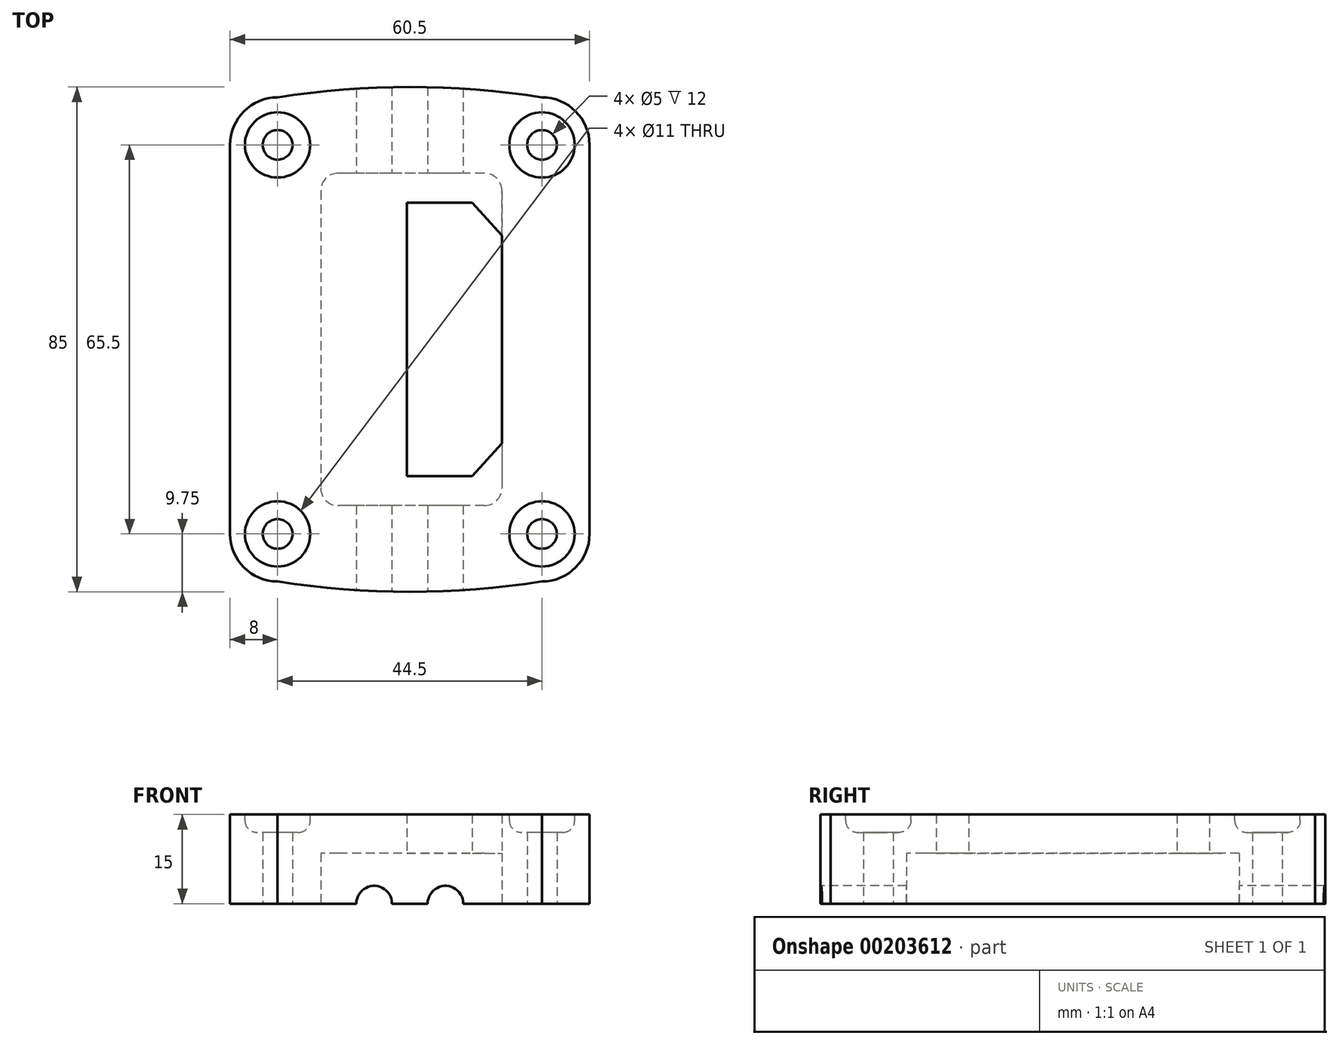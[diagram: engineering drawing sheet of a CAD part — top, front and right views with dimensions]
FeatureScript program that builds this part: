
annotation { "Feature Type Name" : "Feature", "Feature Type Description" : "" }
export const myFeature = defineFeature(function(context is Context, id is Id, definition is map)
    precondition{}
    {
        {
            var Q0;
            Q0=qCreatedBy(makeId("Top.planeOp"),FACE);
            var sketch = newSketch(context, id + "F0", { "sketchPlane" : qUnion([Q0])});
            skPoint(sketch, "E0.middle", {"position": v(0, 0) * mm});
            skCircle(sketch, "E1", {"center": v(22.25, 32.75) * mm, "radius": 2.5 * mm});
            skCircle(sketch, "E2", {"center": v(-22.25, 32.75) * mm, "radius": 2.5 * mm});
            skCircle(sketch, "E3", {"center": v(22.25, -32.75) * mm, "radius": 2.5 * mm});
            skCircle(sketch, "E4", {"center": v(-22.25, -32.75) * mm, "radius": 2.5 * mm});
            skLineSegment(sketch, "E5", {"start": v(30.25, 32.75) * mm, "end": v(30.25, -32.75) * mm});
            skLineSegment(sketch, "E6", {"start": v(-30.25, 32.75) * mm, "end": v(-30.25, -32.75) * mm});
            skArc(sketch, "E7", {"start": v(30.25, 32.75) * mm, "mid": v(27.9, 38.4) * mm, "end": v(22.25, 40.75) * mm});
            skArc(sketch, "E8", {"start": v(-30.25, 32.75) * mm, "mid": v(-27.9, 38.4) * mm, "end": v(-22.25, 40.75) * mm});
            skArc(sketch, "E9", {"start": v(30.25, -32.75) * mm, "mid": v(27.9, -38.4) * mm, "end": v(22.25, -40.75) * mm});
            skArc(sketch, "E10", {"start": v(-30.25, -32.75) * mm, "mid": v(-27.9, -38.4) * mm, "end": v(-22.25, -40.75) * mm});
            skCircle(sketch, "E11", {"center": v(22.25, 32.75) * mm, "radius": 5.5 * mm});
            skCircle(sketch, "E12", {"center": v(-22.25, 32.75) * mm, "radius": 5.5 * mm});
            skCircle(sketch, "E13", {"center": v(22.25, -32.75) * mm, "radius": 5.5 * mm});
            skCircle(sketch, "E14", {"center": v(-22.25, -32.75) * mm, "radius": 5.5 * mm});
            skArc(sketch, "E15", {"start": v(-22.25, -40.75) * mm, "mid": v(0, -42.5) * mm, "end": v(22.25, -40.75) * mm});
            skArc(sketch, "E16", {"start": v(22.25, 40.75) * mm, "mid": v(0, 42.5) * mm, "end": v(-22.25, 40.75) * mm});
            skSolve(sketch);
        }
        {
            var Q0;
            {var subQ6=sQuery(id+"F0.wireOp",EDGE,"DUTKuPmr-ej0r-RtgJ-FTay-jEPyzrQACdq5");var subQ10=sQuery(id+"F0.wireOp",EDGE,"E0.bottom");var subQ13=makeQuery(id+"F0.imprint","INTERSECT",VERTEX,{"derivedFrom":[subQ10,subQ6]});Q0=makeQuery(id+"F0.imprint","IMPRINT",FACE,{"disambiguationData":[TD([[makeQuery(id+"F0.imprint","IMPRINT",EDGE,{"disambiguationData":[TD([[subQ13,-1.0]])],"derivedFrom":subQ10}),1.0]])]});}
            var Q1;
            {var subQ0=sQuery(id+"F0.wireOp",EDGE,"E1");var subQ1=sQuery(id+"F0.wireOp",EDGE,"E0.bottom");var subQ2=makeQuery(id+"F0.imprint","INTERSECT",VERTEX,{"derivedFrom":[subQ1,subQ0]});Q1=makeQuery(id+"F0.imprint","IMPRINT",FACE,{"disambiguationData":[TD([[makeQuery(id+"F0.imprint","IMPRINT",EDGE,{"disambiguationData":[TD([[subQ2,-1.0]])],"derivedFrom":subQ1}),1.0]])]});}
            var Q2;
            {var subQ0=sQuery(id+"F0.wireOp",EDGE,"E7");Q2=makeQuery(id+"F0.imprint","IMPRINT",FACE,{"disambiguationData":[TD([[makeQuery(id+"F0.imprint","IMPRINT",EDGE,{"derivedFrom":subQ0}),1.0]])]});}
            var Q3;
            {var subQ0=sQuery(id+"F0.wireOp",EDGE,"E8");Q3=makeQuery(id+"F0.imprint","IMPRINT",FACE,{"disambiguationData":[TD([[makeQuery(id+"F0.imprint","IMPRINT",EDGE,{"derivedFrom":subQ0}),-1.0]])]});}
            var Q4;
            {var subQ5=sQuery(id+"F0.wireOp",EDGE,"E6");Q4=makeQuery(id+"F0.imprint","IMPRINT",FACE,{"disambiguationData":[TD([[makeQuery(id+"F0.imprint","IMPRINT",EDGE,{"derivedFrom":subQ5}),1.0]])]});}
            var Q5;
            {var subQ12=sQuery(id+"F0.wireOp",EDGE,"E5");Q5=makeQuery(id+"F0.imprint","IMPRINT",FACE,{"disambiguationData":[TD([[makeQuery(id+"F0.imprint","IMPRINT",EDGE,{"derivedFrom":subQ12}),-1.0]])]});}
            var Q6;
            Q6=makeQuery(id+"F0.imprint","IMPRINT",FACE,{"disambiguationData":[TD([[makeQuery(id+"F0.imprint","IMPRINT",EDGE,{"derivedFrom":sQuery(id+"F0.wireOp",EDGE,"E2")}),-1.0]])]});
            var Q7;
            Q7=makeQuery(id+"F0.imprint","IMPRINT",FACE,{"disambiguationData":[TD([[makeQuery(id+"F0.imprint","IMPRINT",EDGE,{"derivedFrom":sQuery(id+"F0.wireOp",EDGE,"E1")}),-1.0]])]});
            var Q8;
            Q8=makeQuery(id+"F0.imprint","IMPRINT",FACE,{"disambiguationData":[TD([[makeQuery(id+"F0.imprint","IMPRINT",EDGE,{"derivedFrom":sQuery(id+"F0.wireOp",EDGE,"E3")}),-1.0]])]});
            var Q9;
            Q9=makeQuery(id+"F0.imprint","IMPRINT",FACE,{"disambiguationData":[TD([[makeQuery(id+"F0.imprint","IMPRINT",EDGE,{"derivedFrom":sQuery(id+"F0.wireOp",EDGE,"E4")}),-1.0]])]});
            extrude(context, id + "F1", {"entities" : qUnion([Q0, Q1, Q2, Q3, Q4, Q5, Q6, Q7, Q8, Q9]), "depth" : 15 * mm});
        }
        {
            var Q0;
            Q0=makeQuery(id+"F1.opExtrude","CAP_FACE",FACE,{"disambiguationData":[OSD([sQuery(id+"F0.wireOp",EDGE,"E1"),sQuery(id+"F0.wireOp",EDGE,"E2"),sQuery(id+"F0.wireOp",EDGE,"E3"),sQuery(id+"F0.wireOp",EDGE,"E4"),sQuery(id+"F0.wireOp",EDGE,"E5"),sQuery(id+"F0.wireOp",EDGE,"E6"),sQuery(id+"F0.wireOp",EDGE,"E7"),sQuery(id+"F0.wireOp",EDGE,"E8"),sQuery(id+"F0.wireOp",EDGE,"E9"),sQuery(id+"F0.wireOp",EDGE,"E10"),sQuery(id+"F0.wireOp",EDGE,"E15"),sQuery(id+"F0.wireOp",EDGE,"E16")])],"isStart":false});
            var sketch = newSketch(context, id + "F2", { "sketchPlane" : qUnion([Q0])});
            skCircle(sketch, "E17.0", {"center": v(-22.25, 32.75) * mm, "radius": 5.5 * mm});
            skCircle(sketch, "E18.0", {"center": v(22.25, 32.75) * mm, "radius": 5.5 * mm});
            skCircle(sketch, "E19.0", {"center": v(-22.25, -32.75) * mm, "radius": 5.5 * mm});
            skCircle(sketch, "E20.0", {"center": v(22.25, -32.75) * mm, "radius": 5.5 * mm});
            skSolve(sketch);
        }
        {
            var Q0;
            Q0=makeQuery(id+"F2.imprint","IMPRINT",FACE,{"disambiguationData":[TD([[makeQuery(id+"F2.imprint","IMPRINT",EDGE,{"derivedFrom":sQuery(id+"F2.wireOp",EDGE,"E17.0")}),1.0]])]});
            var Q1;
            Q1=makeQuery(id+"F2.imprint","IMPRINT",FACE,{"disambiguationData":[TD([[makeQuery(id+"F2.imprint","IMPRINT",EDGE,{"derivedFrom":sQuery(id+"F2.wireOp",EDGE,"E18.0")}),1.0]])]});
            var Q2;
            Q2=makeQuery(id+"F2.imprint","IMPRINT",FACE,{"disambiguationData":[TD([[makeQuery(id+"F2.imprint","IMPRINT",EDGE,{"derivedFrom":sQuery(id+"F2.wireOp",EDGE,"E20.0")}),1.0]])]});
            var Q3;
            Q3=makeQuery(id+"F2.imprint","IMPRINT",FACE,{"disambiguationData":[TD([[makeQuery(id+"F2.imprint","IMPRINT",EDGE,{"derivedFrom":sQuery(id+"F2.wireOp",EDGE,"E19.0")}),1.0]])]});
            extrude(context, id + "F3", {"entities" : qUnion([Q0, Q1, Q2, Q3]), "operationType" : NewBodyOperationType.REMOVE, "oppositeDirection" : true, "depth" : 3 * mm});
        }
        {
            var Q0;
            Q0=qCreatedBy(makeId("Front.planeOp"),FACE);
            var sketch = newSketch(context, id + "F4", { "sketchPlane" : qUnion([Q0])});
            skCircle(sketch, "E21", {"center": v(6, 0) * mm, "radius": 3 * mm});
            skCircle(sketch, "E22", {"center": v(-6, 0) * mm, "radius": 3 * mm});
            skSolve(sketch);
        }
        {
            var Q0;
            Q0=qCreatedBy(makeId("Top.planeOp"),FACE);
            var sketch = newSketch(context, id + "F5", { "sketchPlane" : qUnion([Q0])});
            skLineSegment(sketch, "E23.0", {"start": v(0, 22.5) * mm, "end": v(10.5, 22.5) * mm});
            skLineSegment(sketch, "E24.0", {"start": v(10.5, 22.5) * mm, "end": v(15, 17.5) * mm});
            skLineSegment(sketch, "E25.0", {"start": v(15, 17.5) * mm, "end": v(15, -17.5) * mm});
            skLineSegment(sketch, "E26.0", {"start": v(10.5, -22.5) * mm, "end": v(15, -17.5) * mm});
            skLineSegment(sketch, "E27.0", {"start": v(0, -22.5) * mm, "end": v(10.5, -22.5) * mm});
            skLineSegment(sketch, "E28.0", {"start": v(0, 22.5) * mm, "end": v(0, -22.5) * mm});
            skSolve(sketch);
        }
        {
            var Q0;
            Q0=qCreatedBy(makeId("Top.planeOp"),FACE);
            var sketch = newSketch(context, id + "F6", { "sketchPlane" : qUnion([Q0])});
            skPoint(sketch, "E29.endSnap0", {"position": v(15, 0) * mm});
            skLineSegment(sketch, "E30", {"start": v(-0.5, 0) * mm, "end": v(-0.5, -23) * mm});
            skLineSegment(sketch, "E31", {"start": v(-0.5, 0) * mm, "end": v(-0.5, 23) * mm});
            skLineSegment(sketch, "E32", {"start": v(15.5, 0) * mm, "end": v(15.5, 17.5) * mm});
            skLineSegment(sketch, "E33", {"start": v(15.5, 0) * mm, "end": v(15.5, -17.5) * mm});
            skLineSegment(sketch, "E34", {"start": v(-0.5, -23) * mm, "end": v(10.5, -23) * mm});
            skLineSegment(sketch, "E35", {"start": v(10.5, -23) * mm, "end": v(15.5, -17.5) * mm});
            skLineSegment(sketch, "E36", {"start": v(-0.5, 23) * mm, "end": v(10.5, 23) * mm});
            skLineSegment(sketch, "E37", {"start": v(10.5, 23) * mm, "end": v(15.5, 17.5) * mm});
            skSolve(sketch);
        }
        {
            var Q0;
            Q0=makeQuery(id+"F6.imprint","IMPRINT",FACE,{"disambiguationData":[TD([[makeQuery(id+"F6.imprint","IMPRINT",EDGE,{"derivedFrom":sQuery(id+"F6.wireOp",EDGE,"E30")}),1.0]])]});
            var Q1;
            Q1=makeQuery(id+"F5.imprint","IMPRINT",FACE,{"disambiguationData":[TD([[makeQuery(id+"F5.imprint","IMPRINT",EDGE,{"derivedFrom":sQuery(id+"F5.wireOp",EDGE,"E23.0")}),-1.0]])]});
            extrude(context, id + "F7", {"entities" : qUnion([Q0, Q1]), "operationType" : NewBodyOperationType.REMOVE, "depth" : 16 * mm});
        }
        {
            var Q0;
            Q0=makeQuery(id+"F0.imprint","IMPRINT",FACE,{"disambiguationData":[TD([[makeQuery(id+"F0.imprint","IMPRINT",EDGE,{"derivedFrom":sQuery(id+"F0.wireOp",EDGE,"E5")}),-1.0]])]});
            var sketch = newSketch(context, id + "F8", { "sketchPlane" : qUnion([Q0])});
            skLineSegment(sketch, "E38.0", {"start": v(15.5, 17.5) * mm, "end": v(15.5, -17.5) * mm});
            skLineSegment(sketch, "E39", {"start": v(15.5, -17.5) * mm, "end": v(15.5, -25) * mm});
            skLineSegment(sketch, "E40", {"start": v(12.5, -28) * mm, "end": v(-12, -28) * mm});
            skLineSegment(sketch, "E41", {"start": v(15.5, 17.5) * mm, "end": v(15.5, 25) * mm});
            skLineSegment(sketch, "E42", {"start": v(12.5, 28) * mm, "end": v(-12, 28) * mm});
            skLineSegment(sketch, "E43", {"start": v(-15, 25) * mm, "end": v(-15, -25) * mm});
            skPoint(sketch, "E44.visualSharp", {"position": v(-15, -28) * mm});
            skArc(sketch, "E44.filletArc", {"start": v(-15, -25) * mm, "mid": v(-14.12, -27.12) * mm, "end": v(-12, -28) * mm});
            skPoint(sketch, "E45.visualSharp", {"position": v(15.5, -28) * mm});
            skArc(sketch, "E45.filletArc", {"start": v(12.5, -28) * mm, "mid": v(14.62, -27.12) * mm, "end": v(15.5, -25) * mm});
            skPoint(sketch, "E46.visualSharp", {"position": v(15.5, 28) * mm});
            skArc(sketch, "E46.filletArc", {"start": v(15.5, 25) * mm, "mid": v(14.62, 27.12) * mm, "end": v(12.5, 28) * mm});
            skPoint(sketch, "E47.visualSharp", {"position": v(-15, 28) * mm});
            skArc(sketch, "E47.filletArc", {"start": v(-12, 28) * mm, "mid": v(-14.12, 27.12) * mm, "end": v(-15, 25) * mm});
            skLineSegment(sketch, "E48.0", {"start": v(10.5, -23) * mm, "end": v(15.5, -17.5) * mm});
            skLineSegment(sketch, "E49.0", {"start": v(-0.5, -23) * mm, "end": v(10.5, -23) * mm});
            skLineSegment(sketch, "E50.0", {"start": v(-0.5, -23) * mm, "end": v(-0.5, 23) * mm});
            skLineSegment(sketch, "E51.0", {"start": v(-0.5, 23) * mm, "end": v(10.5, 23) * mm});
            skLineSegment(sketch, "E52.0", {"start": v(10.5, 23) * mm, "end": v(15.5, 17.5) * mm});
            skSolve(sketch);
        }
        {
            var Q0;
            Q0=makeQuery(id+"F8.imprint","IMPRINT",FACE,{"disambiguationData":[TD([[makeQuery(id+"F8.imprint","IMPRINT",EDGE,{"derivedFrom":sQuery(id+"F8.wireOp",EDGE,"E39")}),-1.0]])]});
            extrude(context, id + "F9", {"entities" : qUnion([Q0]), "operationType" : NewBodyOperationType.REMOVE, "depth" : 8.5 * mm});
        }
        {
            var Q0;
            Q0=makeQuery(id+"F3.boolean.opBoolean","COPY",EDGE,{"derivedFrom":makeQuery(id+"F3.opExtrude","CAP_EDGE",EDGE,{"disambiguationData":[OSD([sQuery(id+"F2.wireOp",EDGE,"E19.0")])],"isStart":false})});
            var Q1;
            Q1=makeQuery(id+"F3.boolean.opBoolean","COPY",EDGE,{"derivedFrom":makeQuery(id+"F3.opExtrude","CAP_EDGE",EDGE,{"disambiguationData":[OSD([sQuery(id+"F2.wireOp",EDGE,"E20.0")])],"isStart":false})});
            var Q2;
            Q2=makeQuery(id+"F3.boolean.opBoolean","COPY",EDGE,{"derivedFrom":makeQuery(id+"F3.opExtrude","CAP_EDGE",EDGE,{"disambiguationData":[OSD([sQuery(id+"F2.wireOp",EDGE,"E17.0")])],"isStart":false})});
            var Q3;
            Q3=makeQuery(id+"F3.boolean.opBoolean","COPY",EDGE,{"derivedFrom":makeQuery(id+"F3.opExtrude","CAP_EDGE",EDGE,{"disambiguationData":[OSD([sQuery(id+"F2.wireOp",EDGE,"E18.0")])],"isStart":false})});
            fillet(context, id + "F10", {"entities" : qUnion([Q0, Q1, Q2, Q3]), "radius" : 2 * mm, "tangentPropagation" : true, "allowEdgeOverflow" : false});
        }
        {
            var Q0;
            Q0 = qSketchRegion(id + "F4", true);
            extrude(context, id + "F11", {"entities" : qUnion([Q0]), "operationType" : NewBodyOperationType.REMOVE, "endBound" : BoundingType.SYMMETRIC, "oppositeDirection" : true, "depth" : 86 * mm});
        }
    });
